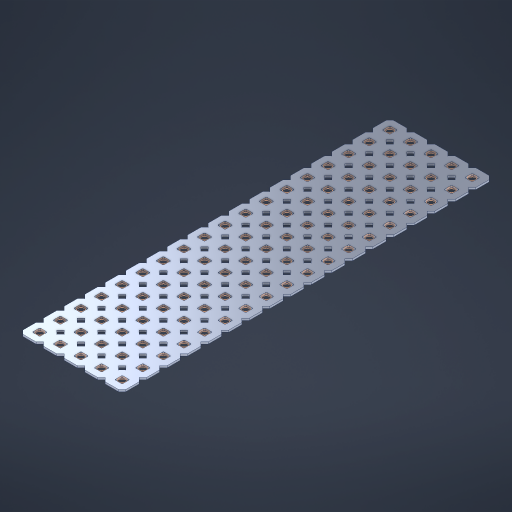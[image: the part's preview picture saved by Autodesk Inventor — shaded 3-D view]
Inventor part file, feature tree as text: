
AUTODESK INVENTOR PART (.ipt)
format: ipt  version: 2023 (Build 270158000, 158)  size: 1,299,968 bytes
history: native  units: in
note: dims shown in document units (in); Inventor stores cm internally (conversion verified against a paired STEP export)
features: other x91, extrude x89, sketch x2, pattern_linear x1
ambient origin geometry x8: Origin, YZ Plane, XZ Plane, XY Plane, X Axis, Y Axis, Z Axis, Center Point
bodies: Solid1 (feature_tree), Body (feature_tree)
feature tree (183):
  pattern_linear  "Rectangular Pattern1"  Spacing1=0.09in  [1 undecoded]
  sketch  "Sketch1"  dims[d1=0.5in]
  sketch  "Sketch2"  dims[d2=0.182in d3=0.09in d4=0.09in d5=0.09in d6=0.09in d7=0.09in d8=0.09in d9=0.09in d10=0.09in d11=0.02in d13=0.0in d14=0.172in d15=0.0625in d16=0.0in d19=0.5in d22=0.5in]
  other  "Srf1"
  other  "Srf126"
  other  "Srf127"
  other  "Srf128"
  other  "Srf129"
  other  "Srf130"
  other  "Srf131"
  other  "Srf250"
  other  "Srf251"
  other  "Srf252"
  other  "Srf253"
  other  "Srf254"
  other  "Srf255"
  other  "Srf256"
  other  "Srf257"
  other  "Srf258"
  other  "Srf259"
  other  "Srf260"
  other  "Srf268"
  other  "Srf269"
  other  "Srf270"
  other  "Srf271"
  other  "Srf272"
  other  "Srf273"
  other  "Srf274"
  other  "Srf275"
  other  "Srf276"
  other  "Srf277"
  other  "Srf278"
  other  "Srf279"
  other  "Srf280"
  other  "Srf281"
  other  "Srf282"
  other  "Srf283"
  other  "Srf284"
  other  "Srf285"
  other  "Srf293"
  other  "Srf294"
  other  "Srf295"
  other  "Srf296"
  other  "Srf297"
  other  "Srf298"
  other  "Srf299"
  other  "Srf300"
  other  "Srf301"
  other  "Srf302"
  other  "Srf303"
  other  "Srf304"
  other  "Srf305"
  other  "Srf306"
  other  "Srf307"
  other  "Srf308"
  other  "Srf309"
  other  "Srf310"
  other  "Srf318"
  other  "Srf319"
  other  "Srf320"
  other  "Srf321"
  other  "Srf322"
  other  "Srf323"
  other  "Srf324"
  other  "Srf325"
  other  "Srf326"
  other  "Srf327"
  other  "Srf328"
  other  "Srf329"
  other  "Srf330"
  other  "Srf331"
  other  "Srf332"
  other  "Srf333"
  other  "Srf334"
  other  "Srf335"
  other  "Srf343"
  other  "Srf344"
  other  "Srf345"
  other  "Srf346"
  other  "Srf347"
  other  "Srf348"
  other  "Srf349"
  other  "Srf350"
  other  "Srf351"
  other  "Srf352"
  other  "Srf353"
  other  "Srf354"
  other  "Srf355"
  other  "Srf356"
  other  "Srf357"
  other  "Srf358"
  other  "Srf359"
  other  "Srf360"
  other  "Circle"
  extrude  "ExtrusionSrf126"  Depth=0.09in
  extrude  "ExtrusionSrf127"  Depth=0.09in
  extrude  "ExtrusionSrf128"  Depth=0.09in
  extrude  "ExtrusionSrf129"  Depth=0.09in
  extrude  "ExtrusionSrf130"  Depth=0.09in
  extrude  "ExtrusionSrf131"  Depth=0.09in
  extrude  "ExtrusionSrf250"  Depth=0.09in
  extrude  "ExtrusionSrf251"  Depth=0.02in
  extrude  "ExtrusionSrf252"  TaperAngle=0.0deg  [1 undecoded]
  extrude  "ExtrusionSrf253"  Depth=0.5in
  extrude  "ExtrusionSrf254"  Depth=0.5in TaperAngle=0.0deg
  extrude  "ExtrusionSrf255"  Depth=0.5in
  extrude  "ExtrusionSrf256"  Depth=0.5in
  extrude  "ExtrusionSrf257"  [1 undecoded]
  extrude  "ExtrusionSrf258"  [1 undecoded]
  extrude  "ExtrusionSrf259"  [1 undecoded]
  extrude  "ExtrusionSrf260"  [1 undecoded]
  extrude  "ExtrusionSrf268"  [1 undecoded]
  extrude  "ExtrusionSrf269"  [1 undecoded]
  extrude  "ExtrusionSrf270"  [1 undecoded]
  extrude  "ExtrusionSrf271"  [1 undecoded]
  extrude  "ExtrusionSrf272"  [1 undecoded]
  extrude  "ExtrusionSrf273"  [1 undecoded]
  extrude  "ExtrusionSrf274"  [1 undecoded]
  extrude  "ExtrusionSrf275"  [1 undecoded]
  extrude  "ExtrusionSrf276"  [1 undecoded]
  extrude  "ExtrusionSrf277"  [1 undecoded]
  extrude  "ExtrusionSrf278"  [1 undecoded]
  extrude  "ExtrusionSrf279"  [1 undecoded]
  extrude  "ExtrusionSrf280"  [1 undecoded]
  extrude  "ExtrusionSrf281"  [1 undecoded]
  extrude  "ExtrusionSrf282"  [1 undecoded]
  extrude  "ExtrusionSrf283"  [1 undecoded]
  extrude  "ExtrusionSrf284"  [1 undecoded]
  extrude  "ExtrusionSrf285"  [1 undecoded]
  extrude  "ExtrusionSrf293"  [1 undecoded]
  extrude  "ExtrusionSrf294"  [1 undecoded]
  extrude  "ExtrusionSrf295"  [1 undecoded]
  extrude  "ExtrusionSrf296"  [1 undecoded]
  extrude  "ExtrusionSrf297"  [1 undecoded]
  extrude  "ExtrusionSrf298"  [1 undecoded]
  extrude  "ExtrusionSrf299"  [1 undecoded]
  extrude  "ExtrusionSrf300"  [1 undecoded]
  extrude  "ExtrusionSrf301"  [1 undecoded]
  extrude  "ExtrusionSrf302"  [1 undecoded]
  extrude  "ExtrusionSrf303"  [1 undecoded]
  extrude  "ExtrusionSrf304"  [1 undecoded]
  extrude  "ExtrusionSrf305"  [1 undecoded]
  extrude  "ExtrusionSrf306"  [1 undecoded]
  extrude  "ExtrusionSrf307"  [1 undecoded]
  extrude  "ExtrusionSrf308"  [1 undecoded]
  extrude  "ExtrusionSrf309"  [1 undecoded]
  extrude  "ExtrusionSrf310"  [1 undecoded]
  extrude  "ExtrusionSrf318"  [1 undecoded]
  extrude  "ExtrusionSrf319"  [1 undecoded]
  extrude  "ExtrusionSrf320"  [1 undecoded]
  extrude  "ExtrusionSrf321"  [1 undecoded]
  extrude  "ExtrusionSrf322"  [1 undecoded]
  extrude  "ExtrusionSrf323"  [1 undecoded]
  extrude  "ExtrusionSrf324"  [1 undecoded]
  extrude  "ExtrusionSrf325"  [1 undecoded]
  extrude  "ExtrusionSrf326"  [1 undecoded]
  extrude  "ExtrusionSrf327"  [1 undecoded]
  extrude  "ExtrusionSrf328"  [1 undecoded]
  extrude  "ExtrusionSrf329"  [1 undecoded]
  extrude  "ExtrusionSrf330"  [1 undecoded]
  extrude  "ExtrusionSrf331"  [1 undecoded]
  extrude  "ExtrusionSrf332"  [1 undecoded]
  extrude  "ExtrusionSrf333"  [1 undecoded]
  extrude  "ExtrusionSrf334"  [1 undecoded]
  extrude  "ExtrusionSrf335"  [1 undecoded]
  extrude  "ExtrusionSrf343"  [1 undecoded]
  extrude  "ExtrusionSrf344"  [1 undecoded]
  extrude  "ExtrusionSrf345"  [1 undecoded]
  extrude  "ExtrusionSrf346"  [1 undecoded]
  extrude  "ExtrusionSrf347"  [1 undecoded]
  extrude  "ExtrusionSrf348"  [1 undecoded]
  extrude  "ExtrusionSrf349"  [1 undecoded]
  extrude  "ExtrusionSrf350"  [1 undecoded]
  extrude  "ExtrusionSrf351"  [1 undecoded]
  extrude  "ExtrusionSrf352"  [1 undecoded]
  extrude  "ExtrusionSrf353"  [1 undecoded]
  extrude  "ExtrusionSrf354"  [1 undecoded]
  extrude  "ExtrusionSrf355"  [1 undecoded]
  extrude  "ExtrusionSrf356"  [1 undecoded]
  extrude  "ExtrusionSrf357"  [1 undecoded]
  extrude  "ExtrusionSrf358"  [1 undecoded]
  extrude  "ExtrusionSrf359"  [1 undecoded]
  extrude  "ExtrusionSrf360"  [1 undecoded]
note: 78 required parameter values undecoded (feature->parameter linkage not recoverable at this tier; creation-order binding heuristic only, values carry confidence <= 0.55)
